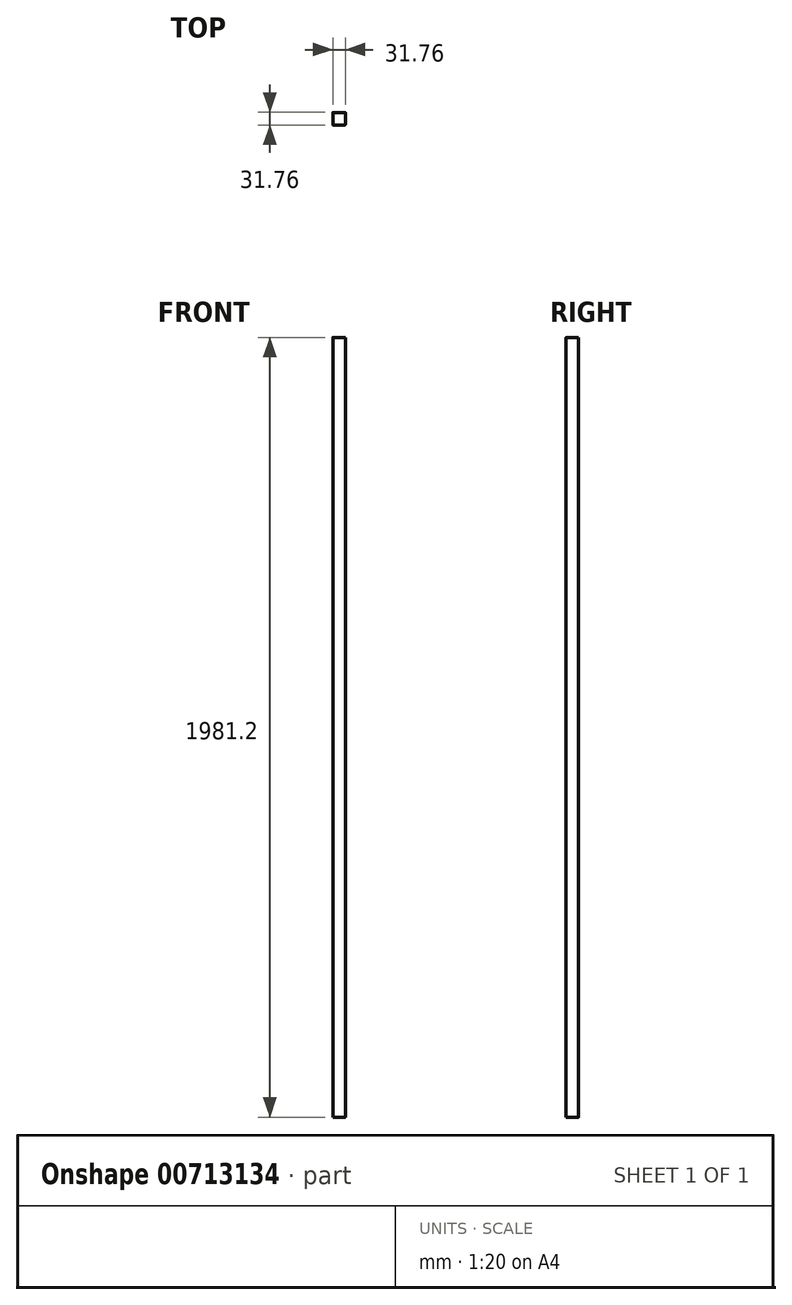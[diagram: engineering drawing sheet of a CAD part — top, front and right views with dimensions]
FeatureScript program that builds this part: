
annotation { "Feature Type Name" : "Feature", "Feature Type Description" : "" }
export const myFeature = defineFeature(function(context is Context, id is Id, definition is map)
    precondition{}
    {
        {
            var Q0;
            Q0=qCreatedBy(makeId("Top.planeOp"),FACE);
            var sketch = newSketch(context, id + "F0", { "sketchPlane" : qUnion([Q0])});
            skLineSegment(sketch, "E0.bottom", {"start": v(15.24, -15.88) * mm, "end": v(-15.24, -15.88) * mm});
            skLineSegment(sketch, "E0.top", {"start": v(15.24, 15.88) * mm, "end": v(-15.24, 15.88) * mm});
            skLineSegment(sketch, "E0.left", {"start": v(15.88, -15.24) * mm, "end": v(15.87, 15.24) * mm});
            skLineSegment(sketch, "E0.right", {"start": v(-15.87, -15.24) * mm, "end": v(-15.88, 15.24) * mm});
            skPoint(sketch, "E0.middle", {"position": v(0, 0) * mm});
            skPoint(sketch, "E1.visualSharp", {"position": v(-15.88, 15.88) * mm});
            skArc(sketch, "E1.filletArc", {"start": v(-15.24, 15.88) * mm, "mid": v(-15.69, 15.69) * mm, "end": v(-15.88, 15.24) * mm});
            skPoint(sketch, "E2.visualSharp", {"position": v(15.87, 15.88) * mm});
            skArc(sketch, "E2.filletArc", {"start": v(15.87, 15.24) * mm, "mid": v(15.69, 15.69) * mm, "end": v(15.24, 15.88) * mm});
            skPoint(sketch, "E3.visualSharp", {"position": v(15.88, -15.88) * mm});
            skArc(sketch, "E3.filletArc", {"start": v(15.24, -15.88) * mm, "mid": v(15.69, -15.69) * mm, "end": v(15.88, -15.24) * mm});
            skPoint(sketch, "E4.visualSharp", {"position": v(-15.87, -15.88) * mm});
            skArc(sketch, "E4.filletArc", {"start": v(-15.87, -15.24) * mm, "mid": v(-15.69, -15.69) * mm, "end": v(-15.24, -15.88) * mm});
            skSolve(sketch);
        }
        {
            var Q0;
            Q0 = qSketchRegion(id + "F0", true);
            extrude(context, id + "F1", {"entities" : qUnion([Q0]), "depth" : 1981.2 * mm, "offsetDistance" : 25.4 * mm});
        }
    });
